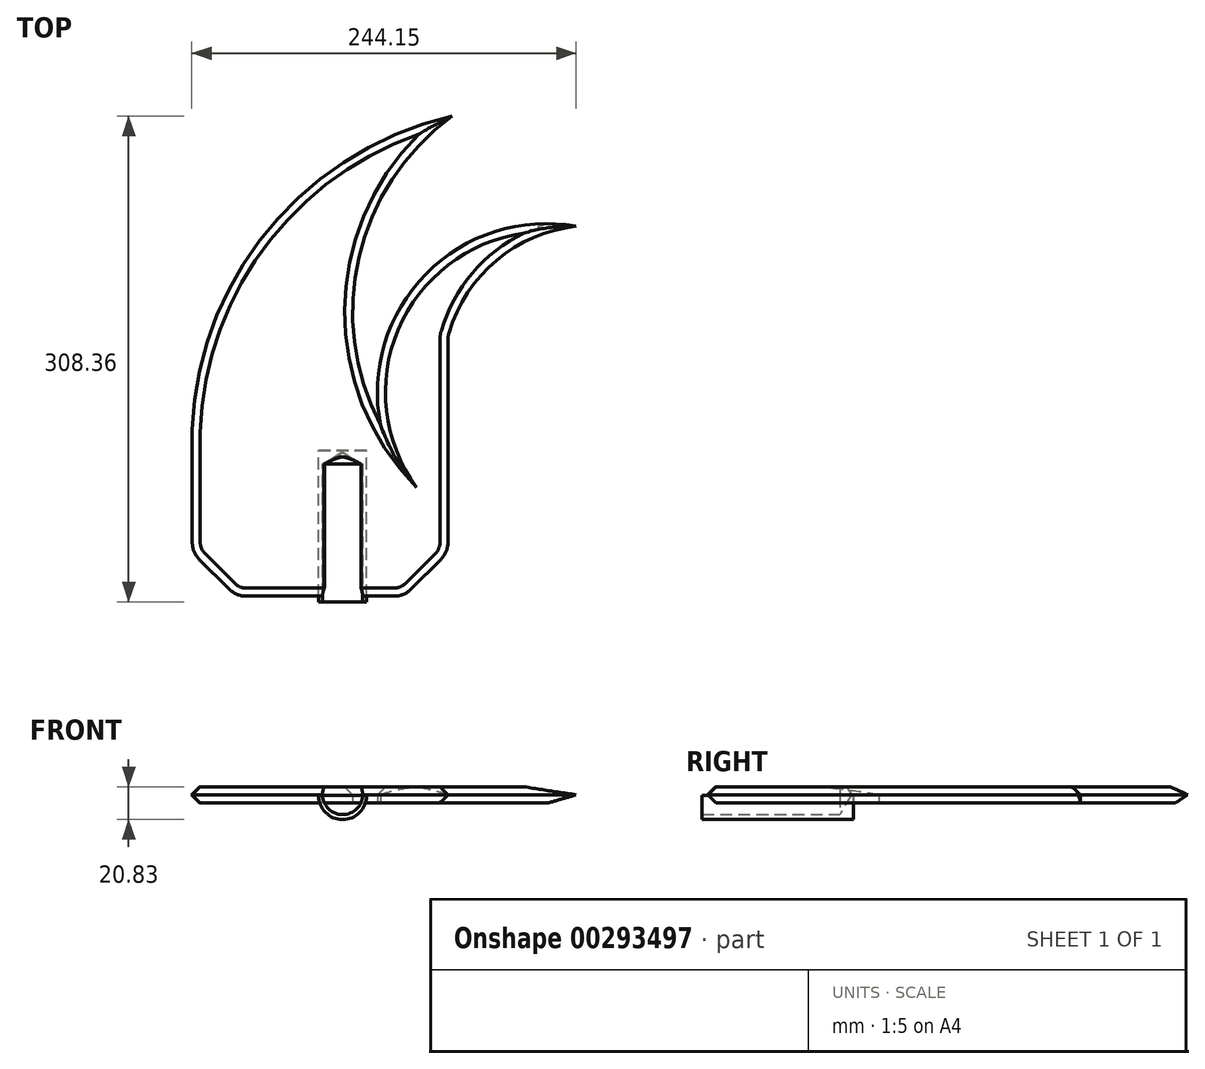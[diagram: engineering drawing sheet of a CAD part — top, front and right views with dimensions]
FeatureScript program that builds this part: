
annotation { "Feature Type Name" : "Feature", "Feature Type Description" : "" }
export const myFeature = defineFeature(function(context is Context, id is Id, definition is map)
    precondition{}
    {
        {
            var Q0;
            Q0=qCreatedBy(makeId("Top.planeOp"),FACE);
            var sketch = newSketch(context, id + "F0", { "sketchPlane" : qUnion([Q0])});
            skLineSegment(sketch, "E0.top", {"start": v(-95.47, -152.4) * mm, "end": v(66.95, -152.4) * mm});
            skLineSegment(sketch, "E0.left", {"start": v(-95.47, -56.2) * mm, "end": v(-95.47, -152.4) * mm});
            skArc(sketch, "E1", {"start": v(148.37, 69.85) * mm, "mid": v(96.88, 47.5) * mm, "end": v(66.95, 0) * mm});
            skArc(sketch, "E2.0", {"start": v(148.37, 69.85) * mm, "mid": v(52.96, 39.58) * mm, "end": v(24.1, -56.26) * mm});
            skLineSegment(sketch, "E3.trimOffspring", {"start": v(66.95, 0) * mm, "end": v(66.95, -152.4) * mm});
            skArc(sketch, "E4.filletArc", {"start": v(-89.12, 139.7) * mm, "mid": v(-93.61, 137.84) * mm, "end": v(-95.47, 133.35) * mm});
            skArc(sketch, "E5", {"start": v(-95.47, -78.94) * mm, "mid": v(-52.85, 60.53) * mm, "end": v(69.63, 139.7) * mm});
            skArc(sketch, "E6.0", {"start": v(24.1, -56.26) * mm, "mid": v(10.37, 50.2) * mm, "end": v(69.63, 139.7) * mm});
            skPoint(sketch, "E7.orphan", {"position": v(148.37, 139.7) * mm});
            skPoint(sketch, "E8.top.end.orphan", {"position": v(148.37, 0) * mm});
            skLineSegment(sketch, "E9", {"start": v(0, -152.4) * mm, "end": v(0, -56.28) * mm});
            skLineSegment(sketch, "E10.left", {"start": v(0, -56.28) * mm, "end": v(0, -152.4) * mm});
            skLineSegment(sketch, "E11.bottom", {"start": v(0, -56.28) * mm, "end": v(15.24, -56.28) * mm});
            skLineSegment(sketch, "E11.top", {"start": v(0, -152.4) * mm, "end": v(15.24, -152.4) * mm});
            skLineSegment(sketch, "E11.right", {"start": v(15.24, -56.28) * mm, "end": v(15.24, -152.4) * mm});
            skSolve(sketch);
        }
        {
            var Q0;
            Q0=makeQuery(id+"F0.imprint","IMPRINT",FACE,{"disambiguationData":[TD([[makeQuery(id+"F0.imprint","IMPRINT",EDGE,{"derivedFrom":sQuery(id+"F0.wireOp",EDGE,"E11.bottom")}),-1.0]])]});
            var Q1;
            Q1=sQuery(id+"F0.wireOp",EDGE,"E10.left");
            revolve(context, id + "F1", {"entities" : qUnion([Q0]), "axis" : qUnion([Q1]), "revolveType" : RevolveType.FULL});
        }
        {
            var Q0;
            Q0 = qSketchRegion(id + "F0", true);
            extrude(context, id + "F2", {"entities" : qUnion([Q0]), "depth" : 17.78 * mm});
        }
        {
            var Q0;
            {var subQ0=sQuery(id+"F0.wireOp",EDGE,"E0.top");Q0=makeQuery(id+"F7.boolean.opBoolean","MERGE",FACE,{"derivedFrom":[makeQuery(id+"F2.opExtrude","CAP_FACE",FACE,{"disambiguationData":[OSD([subQ0,sQuery(id+"F0.wireOp",EDGE,"E0.left"),sQuery(id+"F0.wireOp",EDGE,"E1"),sQuery(id+"F0.wireOp",EDGE,"E2.0"),sQuery(id+"F0.wireOp",EDGE,"E3.trimOffspring"),sQuery(id+"F0.wireOp",EDGE,"E5"),sQuery(id+"F0.wireOp",EDGE,"E6.0")])],"isStart":true}),makeQuery(id+"F7.opExtrude","SWEPT_FACE",FACE,{"disambiguationData":[OSD([subQ0]),TDD([makeQuery(id+"F2.opExtrude","CAP_EDGE",EDGE,{"disambiguationData":[OSD([subQ0])],"isStart":true})])]})]});}
            extrude(context, id + "F3", {"entities" : qUnion([Q0]), "operationType" : NewBodyOperationType.REMOVE, "oppositeDirection" : true, "depth" : 7.62 * mm});
        }
        {
            var Q0;
            Q0=qCreatedBy(makeId("Front.planeOp"),FACE);
            cPlane(context, id + "F4", {"entities" : qUnion([Q0]), "cplaneType" : CPlaneType.OFFSET, "offset" : 152.4 * mm, "width" : 152.4 * mm, "height" : 152.4 * mm});
        }
        {
            var Q0;
            Q0=qCreatedBy(id+"F4.planeOp",FACE);
            var sketch = newSketch(context, id + "F5", { "sketchPlane" : qUnion([Q0])});
            skPoint(sketch, "E12", {"position": v(0, 12.82) * mm});
            skSolve(sketch);
        }
        {
            var Q0;
            Q0=sQuery(id+"F5.wireOp",VERTEX,"E12");
            var Q1;
            Q1=makeQuery(id+"F2.opExtrude","SWEPT_BODY",BODY,{"disambiguationData":[OSD([sQuery(id+"F0.wireOp",EDGE,"E0.top"),sQuery(id+"F0.wireOp",EDGE,"E0.left"),sQuery(id+"F0.wireOp",EDGE,"E1"),sQuery(id+"F0.wireOp",EDGE,"E2.0"),sQuery(id+"F0.wireOp",EDGE,"E3.trimOffspring"),sQuery(id+"F0.wireOp",EDGE,"E5"),sQuery(id+"F0.wireOp",EDGE,"E6.0")])]});
            hole(context, id + "F6", {"style" : HoleStyle.SIMPLE, "endStyle" : HoleEndStyle.BLIND, "holeDiameter" : 25.4 * mm, "holeDepth" : 50.8 * mm, "tappedDepth" : 12.7 * mm, "tapClearance" : 3, "startFromSketch" : true, "locations" : qUnion([Q0]), "scope" : qUnion([Q1])});
        }
        {
            var Q0;
            Q0=makeQuery(id+"F2.opExtrude","SWEPT_FACE",FACE,{"disambiguationData":[OSD([sQuery(id+"F0.wireOp",EDGE,"E0.top")])]});
            extrude(context, id + "F7", {"entities" : qUnion([Q0]), "operationType" : NewBodyOperationType.ADD, "depth" : 12.7 * mm});
        }
        {
            var Q0;
            Q0=makeQuery(id+"F7.opExtrude","CAP_EDGE",EDGE,{"disambiguationData":[OSD([sQuery(id+"F0.wireOp",EDGE,"E0.top"),sQuery(id+"F0.wireOp",EDGE,"E3.trimOffspring")])],"isStart":false});
            var Q1;
            Q1=makeQuery(id+"F7.opExtrude","CAP_EDGE",EDGE,{"disambiguationData":[OSD([sQuery(id+"F0.wireOp",EDGE,"E0.top"),sQuery(id+"F0.wireOp",EDGE,"E0.left")])],"isStart":false});
            chamfer(context, id + "F8", {"entities" : qUnion([Q0, Q1]), "width" : 27.94 * mm, "tangentPropagation" : true});
        }
        {
            var Q0;
            {var subQ0=sQuery(id+"F0.wireOp",EDGE,"E0.top");Q0=makeQuery(id+"F8.opChamfer","BLEND_EDGE",EDGE,{"blendedFrom":[makeQuery(id+"F7.opExtrude","CAP_EDGE",EDGE,{"disambiguationData":[OSD([subQ0,sQuery(id+"F0.wireOp",EDGE,"E0.left")])],"isStart":false}),makeQuery(id+"F7.opExtrude","CAP_FACE",FACE,{"disambiguationData":[OSD([subQ0])],"isStart":false})],"blendedInto":[makeQuery(id+"F7.opExtrude","CAP_FACE",FACE,{"disambiguationData":[OSD([subQ0])],"isStart":false})]});}
            var Q1;
            {var subQ0=sQuery(id+"F0.wireOp",EDGE,"E0.left");var subQ1=sQuery(id+"F0.wireOp",EDGE,"E0.top");Q1=makeQuery(id+"F8.opChamfer","BLEND_EDGE",EDGE,{"blendedFrom":[makeQuery(id+"F7.opExtrude","CAP_EDGE",EDGE,{"disambiguationData":[OSD([subQ1,subQ0])],"isStart":false}),makeQuery(id+"F7.boolean.opBoolean","MERGE",FACE,{"derivedFrom":[makeQuery(id+"F2.opExtrude","SWEPT_FACE",FACE,{"disambiguationData":[OSD([subQ0])]}),makeQuery(id+"F7.opExtrude","SWEPT_FACE",FACE,{"disambiguationData":[OSD([subQ1,subQ0])]})]})],"blendedInto":[makeQuery(id+"F7.boolean.opBoolean","MERGE",FACE,{"derivedFrom":[makeQuery(id+"F2.opExtrude","SWEPT_FACE",FACE,{"disambiguationData":[OSD([subQ0])]}),makeQuery(id+"F7.opExtrude","SWEPT_FACE",FACE,{"disambiguationData":[OSD([subQ1,subQ0])]})]})]});}
            var Q2;
            {var subQ0=sQuery(id+"F0.wireOp",EDGE,"E0.top");Q2=makeQuery(id+"F8.opChamfer","BLEND_EDGE",EDGE,{"blendedFrom":[makeQuery(id+"F7.opExtrude","CAP_EDGE",EDGE,{"disambiguationData":[OSD([subQ0,sQuery(id+"F0.wireOp",EDGE,"E3.trimOffspring")])],"isStart":false}),makeQuery(id+"F7.opExtrude","CAP_FACE",FACE,{"disambiguationData":[OSD([subQ0])],"isStart":false})],"blendedInto":[makeQuery(id+"F7.opExtrude","CAP_FACE",FACE,{"disambiguationData":[OSD([subQ0])],"isStart":false})]});}
            var Q3;
            {var subQ0=sQuery(id+"F0.wireOp",EDGE,"E3.trimOffspring");var subQ1=sQuery(id+"F0.wireOp",EDGE,"E0.top");Q3=makeQuery(id+"F8.opChamfer","BLEND_EDGE",EDGE,{"blendedFrom":[makeQuery(id+"F7.opExtrude","CAP_EDGE",EDGE,{"disambiguationData":[OSD([subQ1,subQ0])],"isStart":false}),makeQuery(id+"F7.boolean.opBoolean","MERGE",FACE,{"derivedFrom":[makeQuery(id+"F2.opExtrude","SWEPT_FACE",FACE,{"disambiguationData":[OSD([subQ0])]}),makeQuery(id+"F7.opExtrude","SWEPT_FACE",FACE,{"disambiguationData":[OSD([subQ1,subQ0])]})]})],"blendedInto":[makeQuery(id+"F7.boolean.opBoolean","MERGE",FACE,{"derivedFrom":[makeQuery(id+"F2.opExtrude","SWEPT_FACE",FACE,{"disambiguationData":[OSD([subQ0])]}),makeQuery(id+"F7.opExtrude","SWEPT_FACE",FACE,{"disambiguationData":[OSD([subQ1,subQ0])]})]})]});}
            var Q4;
            Q4=makeQuery(id+"F2.opExtrude","SWEPT_EDGE",EDGE,{"disambiguationData":[OSD([sQuery(id+"F0.wireOp",EDGE,"E1"),sQuery(id+"F0.wireOp",EDGE,"E3.trimOffspring")])]});
            var Q5;
            Q5=makeQuery(id+"F2.opExtrude","SWEPT_EDGE",EDGE,{"disambiguationData":[OSD([sQuery(id+"F0.wireOp",EDGE,"E0.left"),sQuery(id+"F0.wireOp",EDGE,"E5")])]});
            fillet(context, id + "F9", {"entities" : qUnion([Q0, Q1, Q2, Q3, Q4, Q5]), "radius" : 15.24 * mm, "tangentPropagation" : true, "allowEdgeOverflow" : false});
        }
        {
            var Q0;
            {var subQ0=sQuery(id+"F0.wireOp",EDGE,"E0.left");var subQ1=sQuery(id+"F0.wireOp",EDGE,"E0.top");Q0=makeQuery(id+"F7.boolean.opBoolean","MERGE",EDGE,{"derivedFrom":[makeQuery(id+"F2.opExtrude","CAP_EDGE",EDGE,{"disambiguationData":[OSD([subQ0])],"isStart":false}),makeQuery(id+"F7.opExtrude","SWEPT_EDGE",EDGE,{"disambiguationData":[OSD([subQ1,subQ0]),TDD([makeQuery(id+"F2.opExtrude","CAP_VERTEX",VERTEX,{"disambiguationData":[OSD([subQ1,subQ0])],"isStart":false})])]})]});}
            var Q1;
            Q1=makeQuery(id+"F2.opExtrude","CAP_EDGE",EDGE,{"disambiguationData":[OSD([sQuery(id+"F0.wireOp",EDGE,"E6.0")])],"isStart":false});
            var Q2;
            Q2=makeQuery(id+"F2.opExtrude","CAP_EDGE",EDGE,{"disambiguationData":[OSD([sQuery(id+"F0.wireOp",EDGE,"E2.0")])],"isStart":false});
            var Q3;
            Q3=makeQuery(id+"F2.opExtrude","CAP_EDGE",EDGE,{"disambiguationData":[OSD([sQuery(id+"F0.wireOp",EDGE,"E1")])],"isStart":false});
            var Q4;
            Q4=makeQuery(id+"F2.opExtrude","CAP_EDGE",EDGE,{"disambiguationData":[OSD([sQuery(id+"F0.wireOp",EDGE,"E5")])],"isStart":false});
            var Q5;
            {var subQ0=sQuery(id+"F0.wireOp",EDGE,"E0.top");var subQ2=sQuery(id+"F0.wireOp",EDGE,"E3.trimOffspring");var subQ3=sQuery(id+"F0.wireOp",EDGE,"E1");var subQ4=sQuery(id+"F0.wireOp",EDGE,"E0.left");var subQ5=makeQuery(id+"F2.opExtrude","CAP_FACE",FACE,{"disambiguationData":[OSD([subQ0,subQ4,subQ3,sQuery(id+"F0.wireOp",EDGE,"E2.0"),subQ2,sQuery(id+"F0.wireOp",EDGE,"E5"),sQuery(id+"F0.wireOp",EDGE,"E6.0")])],"isStart":false});var subQ7=makeQuery(id+"F2.opExtrude","CAP_EDGE",EDGE,{"disambiguationData":[OSD([subQ0])],"isStart":false});Q5=makeQuery(id+"F9.opFillet","BLEND_EDGE",EDGE,{"blendedFrom":[makeQuery(id+"F2.opExtrude","SWEPT_EDGE",EDGE,{"disambiguationData":[OSD([subQ3,subQ2])]}),makeQuery(id+"F7.boolean.opBoolean","MERGE",FACE,{"derivedFrom":[subQ5,makeQuery(id+"F7.opExtrude","SWEPT_FACE",FACE,{"disambiguationData":[OSD([subQ0]),TDD([makeQuery(id+"F6.hole-0.boolean.opBoolean","SPLIT",EDGE,{"disambiguationData":[TD([makeQuery(id+"F2.opExtrude","SWEPT_FACE",FACE,{"disambiguationData":[OSD([subQ4])]})])],"derivedFrom":subQ7})])]}),makeQuery(id+"F7.opExtrude","SWEPT_FACE",FACE,{"disambiguationData":[OSD([subQ0]),TDD([makeQuery(id+"F6.hole-0.boolean.opBoolean","SPLIT",EDGE,{"disambiguationData":[TD([makeQuery(id+"F2.opExtrude","SWEPT_FACE",FACE,{"disambiguationData":[OSD([subQ2])]})])],"derivedFrom":subQ7})])]})]})],"blendedInto":[makeQuery(id+"F7.boolean.opBoolean","MERGE",FACE,{"derivedFrom":[subQ5,makeQuery(id+"F7.opExtrude","SWEPT_FACE",FACE,{"disambiguationData":[OSD([subQ0]),TDD([makeQuery(id+"F6.hole-0.boolean.opBoolean","SPLIT",EDGE,{"disambiguationData":[TD([makeQuery(id+"F2.opExtrude","SWEPT_FACE",FACE,{"disambiguationData":[OSD([subQ4])]})])],"derivedFrom":subQ7})])]}),makeQuery(id+"F7.opExtrude","SWEPT_FACE",FACE,{"disambiguationData":[OSD([subQ0]),TDD([makeQuery(id+"F6.hole-0.boolean.opBoolean","SPLIT",EDGE,{"disambiguationData":[TD([makeQuery(id+"F2.opExtrude","SWEPT_FACE",FACE,{"disambiguationData":[OSD([subQ2])]})])],"derivedFrom":subQ7})])]})]})]});}
            var Q6;
            {var subQ0=sQuery(id+"F0.wireOp",EDGE,"E3.trimOffspring");var subQ1=sQuery(id+"F0.wireOp",EDGE,"E0.top");Q6=makeQuery(id+"F7.boolean.opBoolean","MERGE",EDGE,{"derivedFrom":[makeQuery(id+"F2.opExtrude","CAP_EDGE",EDGE,{"disambiguationData":[OSD([subQ0])],"isStart":false}),makeQuery(id+"F7.opExtrude","SWEPT_EDGE",EDGE,{"disambiguationData":[OSD([subQ1,subQ0]),TDD([makeQuery(id+"F2.opExtrude","CAP_VERTEX",VERTEX,{"disambiguationData":[OSD([subQ1,subQ0])],"isStart":false})])]})]});}
            var Q7;
            {var subQ0=sQuery(id+"F0.wireOp",EDGE,"E3.trimOffspring");var subQ1=sQuery(id+"F0.wireOp",EDGE,"E0.top");Q7=makeQuery(id+"F7.boolean.opBoolean","MERGE",EDGE,{"derivedFrom":[makeQuery(id+"F3.boolean.opBoolean","COPY",EDGE,{"derivedFrom":makeQuery(id+"F3.opExtrude","CAP_EDGE",EDGE,{"disambiguationData":[OSD([subQ0])],"isStart":false})}),makeQuery(id+"F7.opExtrude","SWEPT_EDGE",EDGE,{"disambiguationData":[OSD([subQ1,subQ0]),TDD([makeQuery(id+"F3.boolean.opBoolean","COPY",VERTEX,{"derivedFrom":makeQuery(id+"F3.opExtrude","CAP_VERTEX",VERTEX,{"disambiguationData":[OSD([subQ1,subQ0])],"isStart":false})})])]})]});}
            var Q8;
            Q8=makeQuery(id+"F3.boolean.opBoolean","COPY",EDGE,{"derivedFrom":makeQuery(id+"F3.opExtrude","CAP_EDGE",EDGE,{"disambiguationData":[OSD([sQuery(id+"F0.wireOp",EDGE,"E1")])],"isStart":false})});
            var Q9;
            Q9=makeQuery(id+"F3.boolean.opBoolean","COPY",EDGE,{"derivedFrom":makeQuery(id+"F3.opExtrude","CAP_EDGE",EDGE,{"disambiguationData":[OSD([sQuery(id+"F0.wireOp",EDGE,"E2.0")])],"isStart":false})});
            var Q10;
            Q10=makeQuery(id+"F3.boolean.opBoolean","COPY",EDGE,{"derivedFrom":makeQuery(id+"F3.opExtrude","CAP_EDGE",EDGE,{"disambiguationData":[OSD([sQuery(id+"F0.wireOp",EDGE,"E6.0")])],"isStart":false})});
            var Q11;
            Q11=makeQuery(id+"F3.boolean.opBoolean","COPY",EDGE,{"derivedFrom":makeQuery(id+"F3.opExtrude","CAP_EDGE",EDGE,{"disambiguationData":[OSD([sQuery(id+"F0.wireOp",EDGE,"E5")])],"isStart":false})});
            var Q12;
            {var subQ0=sQuery(id+"F0.wireOp",EDGE,"E0.left");var subQ1=sQuery(id+"F0.wireOp",EDGE,"E0.top");Q12=makeQuery(id+"F7.boolean.opBoolean","MERGE",EDGE,{"derivedFrom":[makeQuery(id+"F3.boolean.opBoolean","COPY",EDGE,{"derivedFrom":makeQuery(id+"F3.opExtrude","CAP_EDGE",EDGE,{"disambiguationData":[OSD([subQ0])],"isStart":false})}),makeQuery(id+"F7.opExtrude","SWEPT_EDGE",EDGE,{"disambiguationData":[OSD([subQ1,subQ0]),TDD([makeQuery(id+"F3.boolean.opBoolean","COPY",VERTEX,{"derivedFrom":makeQuery(id+"F3.opExtrude","CAP_VERTEX",VERTEX,{"disambiguationData":[OSD([subQ1,subQ0])],"isStart":false})})])]})]});}
            chamfer(context, id + "F10", {"entities" : qUnion([Q0, Q1, Q2, Q3, Q4, Q5, Q6, Q7, Q8, Q9, Q10, Q11, Q12]), "width" : 5.08 * mm, "tangentPropagation" : true});
        }
        {
            var Q0;
            Q0=makeQuery(id+"F1.opRevolve","SWEPT_BODY",BODY,{"disambiguationData":[OSD([sQuery(id+"F0.wireOp",EDGE,"E10.bottom"),sQuery(id+"F0.wireOp",EDGE,"E10.top"),sQuery(id+"F0.wireOp",EDGE,"E10.left"),sQuery(id+"F0.wireOp",EDGE,"E10.right")])]});
            var Q1;
            Q1=makeQuery(id+"F1.opRevolve","SWEPT_BODY",BODY,{"disambiguationData":[OSD([sQuery(id+"F0.wireOp",EDGE,"E11.bottom"),sQuery(id+"F0.wireOp",EDGE,"E11.top"),sQuery(id+"F0.wireOp",EDGE,"E10.left"),sQuery(id+"F0.wireOp",EDGE,"E11.right")])]});
            transform(context, id + "F11", {"entities" : qUnion([Q0, Q1]), "transformType" : TransformType.TRANSLATION_3D, "dx" : 0 * mm, "dy" : -16.26 * mm, "dz" : 12.2 * mm, "makeCopy" : false});
        }
        {
            var Q0;
            Q0=sQuery(id+"F5.wireOp",VERTEX,"E12");
            var Q1;
            Q1=makeQuery(id+"F1.opRevolve","SWEPT_BODY",BODY,{"disambiguationData":[OSD([sQuery(id+"F0.wireOp",EDGE,"E11.bottom"),sQuery(id+"F0.wireOp",EDGE,"E11.top"),sQuery(id+"F0.wireOp",EDGE,"E10.left"),sQuery(id+"F0.wireOp",EDGE,"E11.right")])]});
            var Q2;
            Q2=makeQuery(id+"F2.opExtrude","SWEPT_BODY",BODY,{"disambiguationData":[OSD([sQuery(id+"F0.wireOp",EDGE,"E0.top"),sQuery(id+"F0.wireOp",EDGE,"E0.left"),sQuery(id+"F0.wireOp",EDGE,"E1"),sQuery(id+"F0.wireOp",EDGE,"E2.0"),sQuery(id+"F0.wireOp",EDGE,"E3.trimOffspring"),sQuery(id+"F0.wireOp",EDGE,"E5"),sQuery(id+"F0.wireOp",EDGE,"E6.0"),sQuery(id+"F0.wireOp",EDGE,"E11.top")])]});
            hole(context, id + "F12", {"style" : HoleStyle.SIMPLE, "endStyle" : HoleEndStyle.BLIND, "oppositeDirection" : true, "holeDiameter" : 25.4 * mm, "holeDepth" : 76.2 * mm, "tappedDepth" : 12.7 * mm, "tapClearance" : 3, "startFromSketch" : true, "locations" : qUnion([Q0]), "scope" : qUnion([Q1, Q2])});
        }
        {
            var Q0;
            Q0=sQuery(id+"F5.wireOp",VERTEX,"E12");
            var Q1;
            Q1=makeQuery(id+"F2.opExtrude","SWEPT_BODY",BODY,{"disambiguationData":[OSD([sQuery(id+"F0.wireOp",EDGE,"E0.top"),sQuery(id+"F0.wireOp",EDGE,"E0.left"),sQuery(id+"F0.wireOp",EDGE,"E1"),sQuery(id+"F0.wireOp",EDGE,"E2.0"),sQuery(id+"F0.wireOp",EDGE,"E3.trimOffspring"),sQuery(id+"F0.wireOp",EDGE,"E5"),sQuery(id+"F0.wireOp",EDGE,"E6.0"),sQuery(id+"F0.wireOp",EDGE,"E11.top")])]});
            var Q2;
            Q2=makeQuery(id+"F1.opRevolve","SWEPT_BODY",BODY,{"disambiguationData":[OSD([sQuery(id+"F0.wireOp",EDGE,"E11.bottom"),sQuery(id+"F0.wireOp",EDGE,"E11.top"),sQuery(id+"F0.wireOp",EDGE,"E10.left"),sQuery(id+"F0.wireOp",EDGE,"E11.right")])]});
            hole(context, id + "F13", {"style" : HoleStyle.SIMPLE, "endStyle" : HoleEndStyle.BLIND, "holeDiameter" : 25.4 * mm, "holeDepth" : 71.12 * mm, "tappedDepth" : 12.7 * mm, "tapClearance" : 3, "startFromSketch" : true, "locations" : qUnion([Q0]), "scope" : qUnion([Q1, Q2])});
        }
    });
